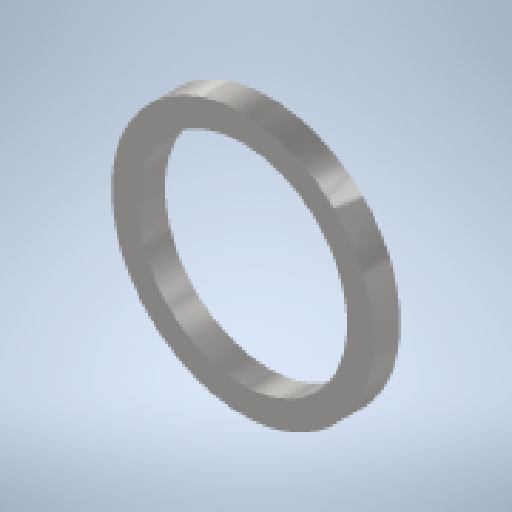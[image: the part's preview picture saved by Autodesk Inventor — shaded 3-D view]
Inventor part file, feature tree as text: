
AUTODESK INVENTOR PART (.ipt)
format: ipt  version: 2024 (Build 280153000, 153)  size: 139,776 bytes
history: native  units: mm
features: other x1, extrude x1, sketch x1
ambient origin geometry x8: Origin, YZ Plane, XZ Plane, XY Plane, X Axis, Y Axis, Z Axis, Center Point
bodies: Body1 (feature_tree)
feature tree (3):
  other  "ソリッド1"
  extrude  "押し出し1"  Depth=100.0mm
  sketch  "スケッチ1"
